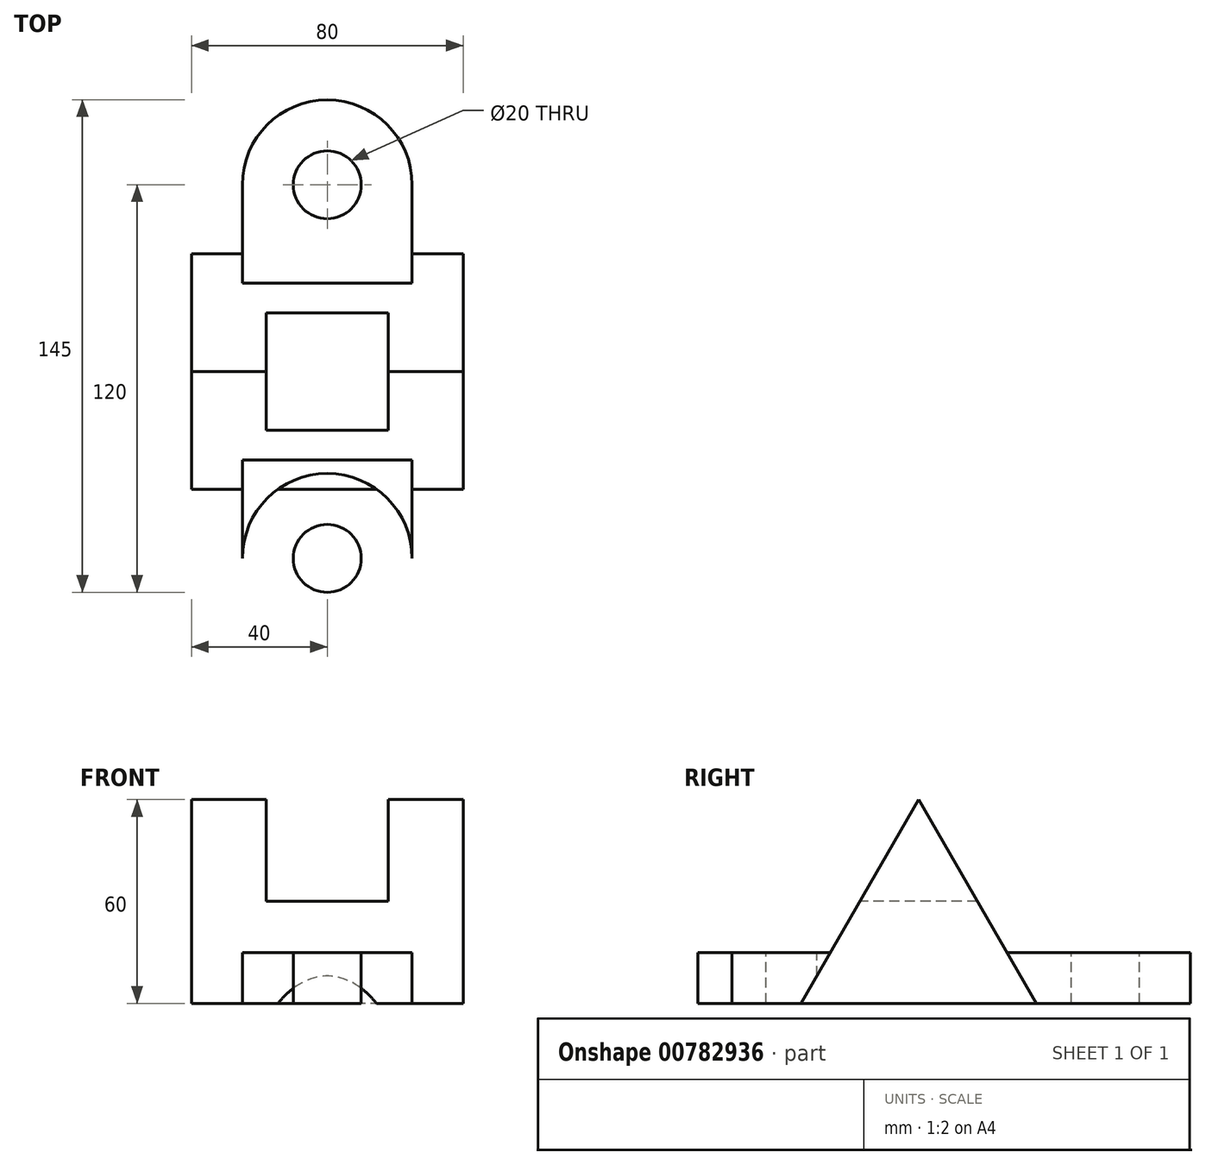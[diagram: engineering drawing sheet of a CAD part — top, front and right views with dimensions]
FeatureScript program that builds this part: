
annotation { "Feature Type Name" : "Feature", "Feature Type Description" : "" }
export const myFeature = defineFeature(function(context is Context, id is Id, definition is map)
    precondition{}
    {
        {
            var Q0;
            Q0=qCreatedBy(makeId("Top.planeOp"),FACE);
            var sketch = newSketch(context, id + "F0", { "sketchPlane" : qUnion([Q0])});
            skCircle(sketch, "E0", {"center": v(0, 55) * mm, "radius": 10 * mm});
            skCircle(sketch, "E1.MirrorC", {"center": v(0, -55) * mm, "radius": 10 * mm});
            skCircle(sketch, "E2", {"center": v(0, 55) * mm, "radius": 25 * mm});
            skCircle(sketch, "E3", {"center": v(0, -55) * mm, "radius": 25 * mm});
            skLineSegment(sketch, "E4", {"start": v(-25, 55) * mm, "end": v(-25, -55) * mm});
            skLineSegment(sketch, "E5", {"start": v(25, 55) * mm, "end": v(25, -55) * mm});
            skSolve(sketch);
        }
        {
            var Q0;
            Q0=makeQuery(id+"F0.imprint","IMPRINT",FACE,{"disambiguationData":[TD([[makeQuery(id+"F0.imprint","IMPRINT",EDGE,{"derivedFrom":sQuery(id+"F0.wireOp",EDGE,"E1.MirrorC")}),1.0]])]});
            var Q1;
            {var subQ0=sQuery(id+"F0.wireOp",EDGE,"E4");Q1=makeQuery(id+"F0.imprint","IMPRINT",FACE,{"disambiguationData":[TD([[makeQuery(id+"F0.imprint","IMPRINT",EDGE,{"derivedFrom":subQ0}),1.0]])]});}
            var Q2;
            Q2=makeQuery(id+"F0.imprint","IMPRINT",FACE,{"disambiguationData":[TD([[makeQuery(id+"F0.imprint","IMPRINT",EDGE,{"derivedFrom":sQuery(id+"F0.wireOp",EDGE,"E0")}),-1.0]])]});
            extrude(context, id + "F1", {"entities" : qUnion([Q0, Q1, Q2]), "oppositeDirection" : true, "depth" : 15 * mm, "offsetDistance" : 25 * mm});
        }
        {
            var Q0;
            Q0=qCreatedBy(makeId("Right.planeOp"),FACE);
            var sketch = newSketch(context, id + "F2", { "sketchPlane" : qUnion([Q0])});
            skCircle(sketch, "E6.cCircle", {"center": v(0, -5) * mm, "radius": 10 * mm, "construction": true});
            skPoint(sketch, "E7.0.midPoint", {"position": v(0, 5) * mm});
            skCircle(sketch, "E8.cCircle", {"center": v(0, 5) * mm, "radius": 20 * mm, "construction": true});
            skLineSegment(sketch, "E8.0", {"start": v(34.64, -15) * mm, "end": v(-34.64, -15) * mm});
            skLineSegment(sketch, "E8.1", {"start": v(-34.64, -15) * mm, "end": v(0, 45) * mm});
            skLineSegment(sketch, "E8.2", {"start": v(0, 45) * mm, "end": v(34.64, -15) * mm});
            skPoint(sketch, "E8.0.midPoint", {"position": v(0, -15) * mm});
            skLineSegment(sketch, "E9", {"start": v(0, -15) * mm, "end": v(0, 5) * mm});
            skSolve(sketch);
        }
        {
            var Q0;
            {var subQ3=sQuery(id+"F2.wireOp",EDGE,"E8.1");Q0=makeQuery(id+"F2.imprint","IMPRINT",FACE,{"disambiguationData":[TD([[makeQuery(id+"F2.imprint","IMPRINT",EDGE,{"derivedFrom":subQ3}),-1.0]])]});}
            extrude(context, id + "F3", {"entities" : qUnion([Q0]), "operationType" : NewBodyOperationType.ADD, "depth" : 40 * mm, "offsetDistance" : 25 * mm, "hasSecondDirection" : true, "secondDirectionOppositeDirection" : true, "secondDirectionDepth" : 40 * mm});
        }
        {
            var Q0;
            Q0=qCreatedBy(makeId("Front.planeOp"),FACE);
            var sketch = newSketch(context, id + "F4", { "sketchPlane" : qUnion([Q0])});
            skLineSegment(sketch, "E10.bottom", {"start": v(18, 45) * mm, "end": v(-18, 45) * mm});
            skLineSegment(sketch, "E10.top", {"start": v(18, 15) * mm, "end": v(-18, 15) * mm});
            skLineSegment(sketch, "E10.left", {"start": v(18, 45) * mm, "end": v(18, 15) * mm});
            skLineSegment(sketch, "E10.right", {"start": v(-18, 45) * mm, "end": v(-18, 15) * mm});
            skSolve(sketch);
        }
        {
            var Q0;
            Q0 = qSketchRegion(id + "F4", true);
            extrude(context, id + "F5", {"entities" : qUnion([Q0]), "operationType" : NewBodyOperationType.REMOVE, "oppositeDirection" : true, "depth" : 50 * mm, "offsetDistance" : 25 * mm, "hasSecondDirection" : true, "secondDirectionOppositeDirection" : false, "secondDirectionDepth" : 25 * mm});
        }
    });
